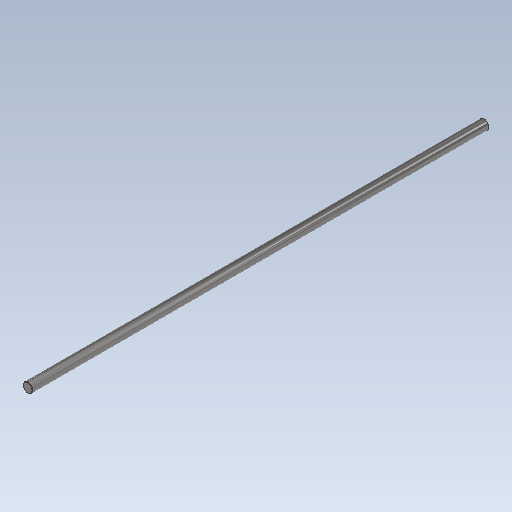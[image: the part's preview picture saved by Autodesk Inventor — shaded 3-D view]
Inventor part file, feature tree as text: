
AUTODESK INVENTOR PART (.ipt)
format: ipt  version: 2020 (Build 240168000, 168)  size: 119,808 bytes
history: native  units: mm
features: other x1, extrude x1, chamfer x1, sketch x1
ambient origin geometry x8: Origin, YZ Plane, XZ Plane, XY Plane, X Axis, Y Axis, Z Axis, Center Point
bodies: Body1 (feature_tree)
feature tree (4):
  other  "Bryła1"
  extrude  "Wyciągnięcie proste1"  Depth=12.0mm
  chamfer  "Faza1"  Distance=564.0mm
  sketch  "Szkic1"
